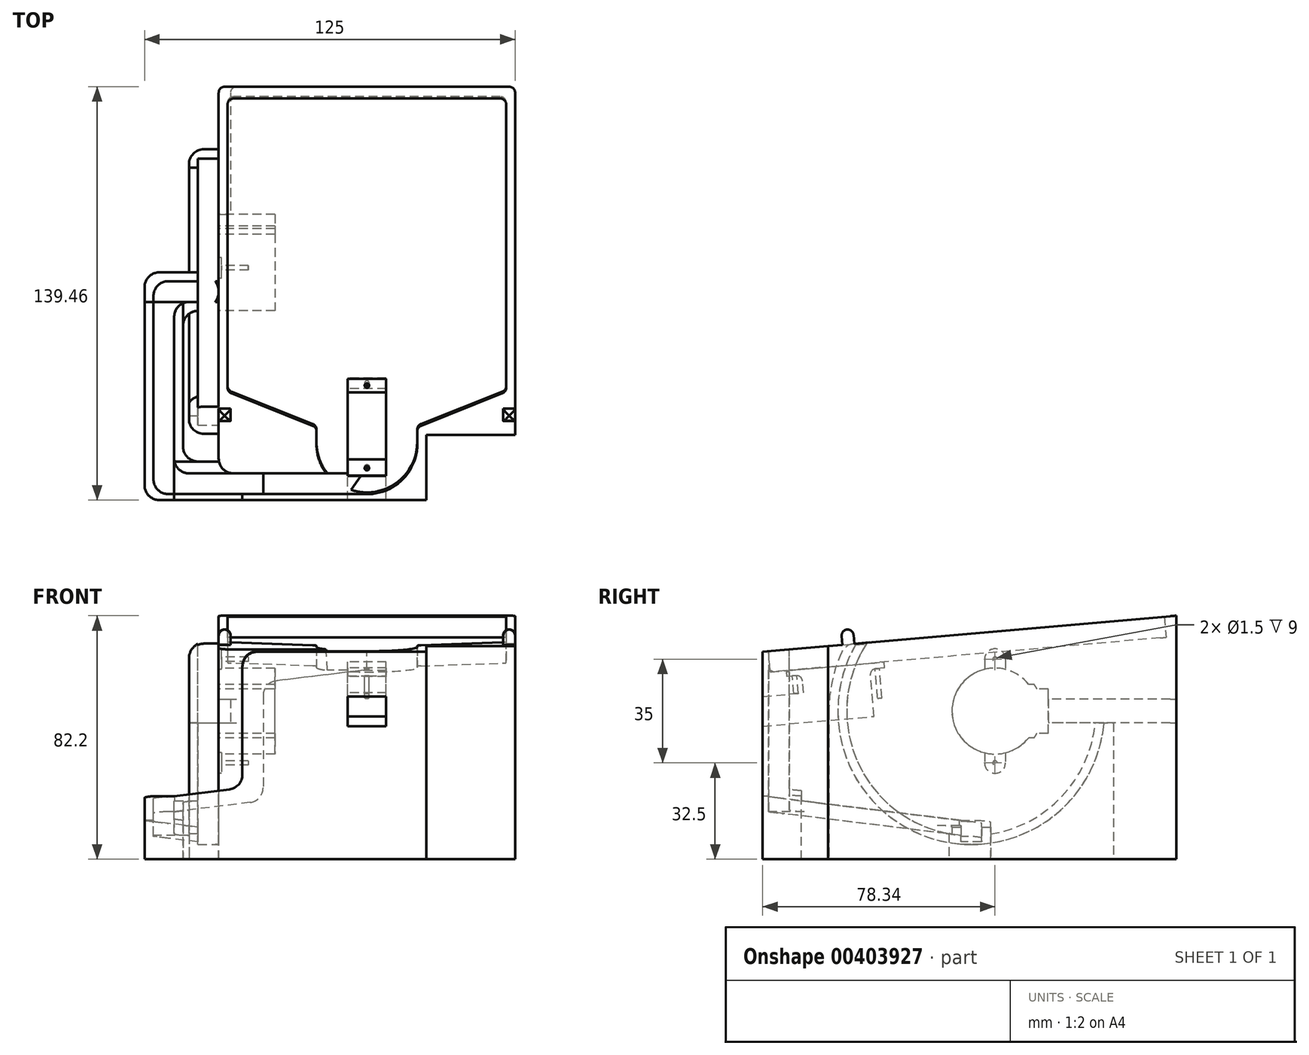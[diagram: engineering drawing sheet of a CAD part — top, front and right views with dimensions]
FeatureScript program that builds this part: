
annotation { "Feature Type Name" : "Feature", "Feature Type Description" : "" }
export const myFeature = defineFeature(function(context is Context, id is Id, definition is map)
    precondition{}
    {
        {
            var Q0;
            Q0=qCreatedBy(makeId("Right.planeOp"),FACE);
            var sketch = newSketch(context, id + "F0", { "sketchPlane" : qUnion([Q0])});
            skLineSegment(sketch, "E0", {"start": v(-65.34, 50) * mm, "end": v(-65.34, -20) * mm});
            skLineSegment(sketch, "E1", {"start": v(-65.34, -20) * mm, "end": v(74.12, -20) * mm});
            skLineSegment(sketch, "E2", {"start": v(74.12, -20) * mm, "end": v(74.12, 62.2) * mm});
            skLineSegment(sketch, "E3", {"start": v(74.12, 62.2) * mm, "end": v(-65.34, 50) * mm});
            skPoint(sketch, "E4", {"position": v(0, 55.72) * mm});
            skPoint(sketch, "E5", {"position": v(0, 48.7) * mm});
            skSolve(sketch);
        }
        {
            var Q0;
            Q0=qSketchRegion(id+"F0",true);
            extrude(context, id + "F1", {"entities" : qUnion([Q0]), "depth" : 50 * mm, "hasSecondDirection" : true, "secondDirectionOppositeDirection" : true, "secondDirectionDepth" : 50 * mm});
        }
        {
            var Q0;
            Q0=makeQuery(id+"F1.opExtrude","SWEPT_FACE",FACE,{"disambiguationData":[OSD([sQuery(id+"F0.wireOp",EDGE,"E3")])]});
            var sketch = newSketch(context, id + "F2", { "sketchPlane" : qUnion([Q0])});
            skPoint(sketch, "E6.endSnap0", {"position": v(0, -57.54) * mm});
            skPoint(sketch, "E6.end.orphan", {"position": v(0, -83) * mm});
            skPoint(sketch, "E7.orphan", {"position": v(-48, -57.54) * mm});
            skPoint(sketch, "E8.orphan", {"position": v(48, -57.54) * mm});
            skLineSegment(sketch, "E9.0", {"start": v(47, 75.26) * mm, "end": v(-47, 75.26) * mm});
            skLineSegment(sketch, "E9.1", {"start": v(47, 75.26) * mm, "end": v(47, -24.06) * mm});
            skLineSegment(sketch, "E9.2", {"start": v(-47, 75.26) * mm, "end": v(-47, -24.06) * mm});
            skLineSegment(sketch, "E9.3", {"start": v(17, -36.06) * mm, "end": v(47, -24.06) * mm});
            skLineSegment(sketch, "E9.4", {"start": v(-17, -36.06) * mm, "end": v(-47, -24.06) * mm});
            skLineSegment(sketch, "E9.5", {"start": v(-17, -41.74) * mm, "end": v(-17, -36.06) * mm});
            skArc(sketch, "E9.6", {"start": v(-17, -41.74) * mm, "mid": v(0, -58.74) * mm, "end": v(17, -41.74) * mm});
            skLineSegment(sketch, "E9.7", {"start": v(17, -41.74) * mm, "end": v(17, -36.06) * mm});
            skPoint(sketch, "E10.bottom.end.orphan", {"position": v(-48, 78.46) * mm});
            skPoint(sketch, "E10.bottom.start.orphan", {"position": v(48, 78.46) * mm});
            skPoint(sketch, "E11", {"position": v(0, 4.86) * mm});
            skSolve(sketch);
        }
        {
            var Q0;
            Q0=makeQuery(id+"F2.imprint","IMPRINT",FACE,{"disambiguationData":[TD([[makeQuery(id+"F2.imprint","IMPRINT",EDGE,{"derivedFrom":sQuery(id+"F2.wireOp",EDGE,"E9.0")}),1.0]])]});
            cPlane(context, id + "F3", {"entities" : qUnion([Q0]), "cplaneType" : CPlaneType.OFFSET, "offset" : 7 * mm, "oppositeDirection" : true, "width" : 150 * mm, "height" : 150 * mm});
        }
        {
            var Q0;
            Q0=qCreatedBy(id+"F3.planeOp",FACE);
            var sketch = newSketch(context, id + "F4", { "sketchPlane" : qUnion([Q0])});
            skPoint(sketch, "E12", {"position": v(0, 4.24) * mm});
            skPoint(sketch, "E13.endSnap0", {"position": v(0, -58.41) * mm});
            skPoint(sketch, "E13.end.orphan", {"position": v(0, -83.88) * mm});
            skPoint(sketch, "E14.orphan", {"position": v(-48, -58.41) * mm});
            skPoint(sketch, "E15.orphan", {"position": v(48, -58.41) * mm});
            skLineSegment(sketch, "E16.0", {"start": v(47, 75.26) * mm, "end": v(-47, 75.26) * mm});
            skLineSegment(sketch, "E16.1", {"start": v(47, 75.26) * mm, "end": v(47, -24.06) * mm});
            skLineSegment(sketch, "E16.2", {"start": v(-47, 75.26) * mm, "end": v(-47, -24.06) * mm});
            skLineSegment(sketch, "E16.3", {"start": v(17, -36.06) * mm, "end": v(47, -24.06) * mm});
            skLineSegment(sketch, "E16.4", {"start": v(-17, -36.06) * mm, "end": v(-47, -24.06) * mm});
            skLineSegment(sketch, "E16.5", {"start": v(-17, -41.74) * mm, "end": v(-17, -36.06) * mm});
            skArc(sketch, "E16.6", {"start": v(-17, -41.74) * mm, "mid": v(0, -58.74) * mm, "end": v(17, -41.74) * mm});
            skLineSegment(sketch, "E16.7", {"start": v(17, -41.74) * mm, "end": v(17, -36.06) * mm});
            skPoint(sketch, "E17.bottom.end.orphan", {"position": v(-48, 77.59) * mm});
            skPoint(sketch, "E17.bottom.start.orphan", {"position": v(48, 77.59) * mm});
            skSolve(sketch);
        }
        {
            var Q1;
            Q1=qSketchRegion(id+"F2",true);
            var Q2;
            Q2=qSketchRegion(id+"F4",true);
            loft(context, id + "F5", {"operationType" : NewBodyOperationType.REMOVE, "sheetProfilesArray" : [{ "sheetProfileEntities" : qUnion([Q1]) }, { "sheetProfileEntities" : qUnion([Q2]) }]});
        }
        {
            var Q0;
            Q0=makeQuery(id+"F1.opExtrude","CAP_FACE",FACE,{"disambiguationData":[OSD([sQuery(id+"F0.wireOp",EDGE,"E0"),sQuery(id+"F0.wireOp",EDGE,"E1"),sQuery(id+"F0.wireOp",EDGE,"E2"),sQuery(id+"F0.wireOp",EDGE,"E3")])],"isStart":true});
            var sketch = newSketch(context, id + "F6", { "sketchPlane" : qUnion([Q0])});
            skArc(sketch, "E18", {"start": v(-24.37, 21) * mm, "mid": v(1.5, 30) * mm, "end": v(-24.37, 39) * mm});
            skPoint(sketch, "E19", {"position": v(-5, 30) * mm});
            skLineSegment(sketch, "E20.bottom", {"start": v(-31, 22.5) * mm, "end": v(-27.13, 22.5) * mm});
            skLineSegment(sketch, "E20.top", {"start": v(-31, 37.5) * mm, "end": v(-27.13, 37.5) * mm});
            skLineSegment(sketch, "E20.left", {"start": v(-31, 22.5) * mm, "end": v(-31, 37.5) * mm});
            skArc(sketch, "E21", {"start": v(-26.23, 39) * mm, "mid": v(-26.7, 38.26) * mm, "end": v(-27.13, 37.5) * mm});
            skLineSegment(sketch, "E22.bottom", {"start": v(-26.23, 39) * mm, "end": v(-24.37, 39) * mm});
            skLineSegment(sketch, "E22.top", {"start": v(-26.23, 21) * mm, "end": v(-24.37, 21) * mm});
            skArc(sketch, "E23.trimOffspring", {"start": v(-27.13, 22.5) * mm, "mid": v(-26.7, 21.74) * mm, "end": v(-26.23, 21) * mm});
            skSolve(sketch);
        }
        {
            var Q0;
            Q0=qSketchRegion(id+"F6",true);
            extrude(context, id + "F7", {"entities" : qUnion([Q0]), "operationType" : NewBodyOperationType.REMOVE, "oppositeDirection" : true, "depth" : 19 * mm});
        }
        {
            var Q0;
            Q0=makeQuery(id+"F1.opExtrude","CAP_FACE",FACE,{"disambiguationData":[OSD([sQuery(id+"F0.wireOp",EDGE,"E0"),sQuery(id+"F0.wireOp",EDGE,"E1"),sQuery(id+"F0.wireOp",EDGE,"E2"),sQuery(id+"F0.wireOp",EDGE,"E3")])],"isStart":true});
            var sketch = newSketch(context, id + "F8", { "sketchPlane" : qUnion([Q0])});
            skLineSegment(sketch, "E24", {"start": v(-13, 47.5) * mm, "end": v(-13, 12.5) * mm});
            skPoint(sketch, "E25", {"position": v(-13, 30) * mm});
            skArc(sketch, "E26.0.startCap", {"start": v(-16.5, 47.5) * mm, "mid": v(-13, 51) * mm, "end": v(-9.5, 47.5) * mm});
            skArc(sketch, "E26.0.endCap", {"start": v(-9.5, 12.5) * mm, "mid": v(-13, 9) * mm, "end": v(-16.5, 12.5) * mm});
            skLineSegment(sketch, "E26.0.left", {"start": v(-9.5, 47.5) * mm, "end": v(-9.5, 12.5) * mm});
            skLineSegment(sketch, "E26.0.right", {"start": v(-16.5, 47.5) * mm, "end": v(-16.5, 12.5) * mm});
            skSolve(sketch);
        }
        {
            var Q0;
            Q0=qSketchRegion(id+"F8",true);
            extrude(context, id + "F9", {"entities" : qUnion([Q0]), "operationType" : NewBodyOperationType.REMOVE, "oppositeDirection" : true, "depth" : 1 * mm});
        }
        {
            var Q0;
            Q0=makeQuery(id+"F1.opExtrude","CAP_FACE",FACE,{"disambiguationData":[OSD([sQuery(id+"F0.wireOp",EDGE,"E0"),sQuery(id+"F0.wireOp",EDGE,"E1"),sQuery(id+"F0.wireOp",EDGE,"E2"),sQuery(id+"F0.wireOp",EDGE,"E3")])],"isStart":true});
            var sketch = newSketch(context, id + "F10", { "sketchPlane" : qUnion([Q0])});
            skLineSegment(sketch, "E27.bottom", {"start": v(-81, 34) * mm, "end": v(-21, 34) * mm});
            skLineSegment(sketch, "E27.top", {"start": v(-81, 26) * mm, "end": v(-21, 26) * mm});
            skLineSegment(sketch, "E27.left", {"start": v(-81, 34) * mm, "end": v(-81, 26) * mm});
            skLineSegment(sketch, "E27.right", {"start": v(-21, 34) * mm, "end": v(-21, 26) * mm});
            skPoint(sketch, "E27.middle", {"position": v(-51, 30) * mm});
            skSolve(sketch);
        }
        {
            var Q0;
            Q0=qSketchRegion(id+"F10",true);
            extrude(context, id + "F11", {"entities" : qUnion([Q0]), "operationType" : NewBodyOperationType.REMOVE, "oppositeDirection" : true, "depth" : 4 * mm});
        }
        {
            var Q0;
            Q0=qCreatedBy(makeId("Front.planeOp"),FACE);
            cPlane(context, id + "F12", {"entities" : qUnion([Q0]), "cplaneType" : CPlaneType.OFFSET, "offset" : 5 * mm, "oppositeDirection" : true, "width" : 150 * mm, "height" : 150 * mm});
        }
        {
            var Q0;
            Q0=qCreatedBy(id+"F12.planeOp",FACE);
            var sketch = newSketch(context, id + "F13", { "sketchPlane" : qUnion([Q0])});
            skLineSegment(sketch, "E28", {"start": v(-50, -20) * mm, "end": v(-75, -20) * mm});
            skLineSegment(sketch, "E29", {"start": v(-50, -9.96) * mm, "end": v(-75, -6.9) * mm});
            skLineSegment(sketch, "E30", {"start": v(-75, -20) * mm, "end": v(-75, -6.9) * mm});
            skLineSegment(sketch, "E31", {"start": v(-50, -20) * mm, "end": v(-50, -9.96) * mm});
            skSolve(sketch);
        }
        {
            var Q0;
            Q0=qSketchRegion(id+"F13",true);
            extrude(context, id + "F14", {"entities" : qUnion([Q0]), "operationType" : NewBodyOperationType.ADD, "depth" : 6.5 * mm, "hasSecondDirection" : true, "secondDirectionOppositeDirection" : true, "secondDirectionDepth" : 6.5 * mm});
        }
        {
            var Q0;
            Q0=makeQuery(id+"F2.imprint","IMPRINT",FACE,{"disambiguationData":[TD([[makeQuery(id+"F2.imprint","IMPRINT",EDGE,{"derivedFrom":sQuery(id+"F2.wireOp",EDGE,"E9.0")}),1.0]])]});
            var sketch = newSketch(context, id + "F15", { "sketchPlane" : qUnion([Q0])});
            skLineSegment(sketch, "E32.bottom", {"start": v(6.5, -48.24) * mm, "end": v(-6.5, -48.24) * mm});
            skLineSegment(sketch, "E32.top", {"start": v(6.5, -25.24) * mm, "end": v(-6.5, -25.24) * mm});
            skLineSegment(sketch, "E32.left", {"start": v(6.5, -48.24) * mm, "end": v(6.5, -25.24) * mm});
            skLineSegment(sketch, "E32.right", {"start": v(-6.5, -48.24) * mm, "end": v(-6.5, -25.24) * mm});
            skPoint(sketch, "E32.middle", {"position": v(0, -36.74) * mm});
            skSolve(sketch);
        }
        {
            var Q0;
            Q0=qSketchRegion(id+"F15",true);
            extrude(context, id + "F16", {"entities" : qUnion([Q0]), "operationType" : NewBodyOperationType.REMOVE, "oppositeDirection" : true, "depth" : 25 * mm});
        }
        {
            var Q0;
            Q0=makeQuery(id+"F2.imprint","IMPRINT",FACE,{"disambiguationData":[TD([[makeQuery(id+"F2.imprint","IMPRINT",EDGE,{"derivedFrom":sQuery(id+"F2.wireOp",EDGE,"E9.0")}),1.0]])]});
            var sketch = newSketch(context, id + "F17", { "sketchPlane" : qUnion([Q0])});
            skLineSegment(sketch, "E33.bottom", {"start": v(6.5, -20.24) * mm, "end": v(-6.5, -20.24) * mm});
            skLineSegment(sketch, "E33.top", {"start": v(6.5, -53.24) * mm, "end": v(-6.5, -53.24) * mm});
            skLineSegment(sketch, "E33.left", {"start": v(6.5, -20.24) * mm, "end": v(6.5, -53.24) * mm});
            skLineSegment(sketch, "E33.right", {"start": v(-6.5, -20.24) * mm, "end": v(-6.5, -53.24) * mm});
            skPoint(sketch, "E33.middle", {"position": v(0, -36.74) * mm});
            skSolve(sketch);
        }
        {
            var Q0;
            Q0=qSketchRegion(id+"F17",true);
            extrude(context, id + "F18", {"entities" : qUnion([Q0]), "operationType" : NewBodyOperationType.REMOVE, "oppositeDirection" : true, "depth" : 9 * mm});
        }
        {
            var Q0;
            Q0=makeQuery(id+"FUqeBeKpT4LYNuk_1.boolean.opBoolean","MERGE",FACE,{"derivedFrom":[makeQuery(id+"F1.opExtrude","SWEPT_FACE",FACE,{"disambiguationData":[OSD([sQuery(id+"F0.wireOp",EDGE,"E0")])]}),makeQuery(id+"F61UTTqEWsXgY2D_1.opExtrude","SWEPT_FACE",FACE,{"disambiguationData":[OSD([sQuery(id+"F9Du9WT9e9JY5Dl_1.wireOp",EDGE,"sJgd1tPc-9qsz-vVnT-TqeQ-4TYIqpoZbmCu")])]}),makeQuery(id+"FUqeBeKpT4LYNuk_1.opExtrude","CAP_FACE",FACE,{"disambiguationData":[OSD([sQuery(id+"Fu5qXJoa0auTo1w_1.wireOp",EDGE,"depduNjt-3aMR-BOii-vv3o-0Txvqa5xbjUM"),sQuery(id+"Fu5qXJoa0auTo1w_1.wireOp",EDGE,"YClS0oY7-eXia-WmQ4-NOUT-qmrgQAcRW2ul"),sQuery(id+"Fu5qXJoa0auTo1w_1.wireOp",EDGE,"FjPESpCu-MEkZ-X1k0-rLkk-jPPFp3MV8du9"),sQuery(id+"Fu5qXJoa0auTo1w_1.wireOp",EDGE,"T3NzeVoH-fv4R-7HJz-S144-zwuEIWOQCuFN")])],"isStart":true})]});
            var sketch = newSketch(context, id + "F19", { "sketchPlane" : qUnion([Q0])});
            skLineSegment(sketch, "E34.bottom", {"start": v(50, -20) * mm, "end": v(20, -20) * mm});
            skLineSegment(sketch, "E34.top", {"start": v(50, 60) * mm, "end": v(20, 60) * mm});
            skLineSegment(sketch, "E34.left", {"start": v(50, -20) * mm, "end": v(50, 60) * mm});
            skLineSegment(sketch, "E34.right", {"start": v(20, -20) * mm, "end": v(20, 60) * mm});
            skSolve(sketch);
        }
        {
            var Q0;
            Q0=qSketchRegion(id+"F19",true);
            extrude(context, id + "F20", {"entities" : qUnion([Q0]), "operationType" : NewBodyOperationType.REMOVE, "oppositeDirection" : true, "depth" : 22 * mm});
        }
        {
            var Q0;
            Q0=makeQuery(id+"F16.boolean.opBoolean","COPY",FACE,{"derivedFrom":makeQuery(id+"F16.opExtrude","SWEPT_FACE",FACE,{"disambiguationData":[OSD([sQuery(id+"F15.wireOp",EDGE,"E32.bottom")])]})});
            var sketch = newSketch(context, id + "F21", { "sketchPlane" : qUnion([Q0])});
            skLineSegment(sketch, "E35.bottom", {"start": v(-6.5, 30.5) * mm, "end": v(6.5, 30.5) * mm});
            skLineSegment(sketch, "E35.top", {"start": v(-6.5, 40.5) * mm, "end": v(6.5, 40.5) * mm});
            skLineSegment(sketch, "E35.left", {"start": v(-6.5, 30.5) * mm, "end": v(-6.5, 40.5) * mm});
            skLineSegment(sketch, "E35.right", {"start": v(6.5, 30.5) * mm, "end": v(6.5, 40.5) * mm});
            skSolve(sketch);
        }
        {
            var Q0;
            Q0=qSketchRegion(id+"F21",true);
            extrude(context, id + "F22", {"entities" : qUnion([Q0]), "operationType" : NewBodyOperationType.REMOVE, "oppositeDirection" : true, "depth" : 25 * mm});
        }
        {
            var Q0;
            Q0=qCreatedBy(id+"F12.planeOp",FACE);
            var sketch = newSketch(context, id + "F23", { "sketchPlane" : qUnion([Q0])});
            skLineSegment(sketch, "E36", {"start": v(-50, -6.3) * mm, "end": v(-50, -15) * mm});
            skLineSegment(sketch, "E37", {"start": v(-50, -15) * mm, "end": v(-72, -12.3) * mm});
            skLineSegment(sketch, "E38", {"start": v(-72, -12.3) * mm, "end": v(-72, -6.3) * mm});
            skLineSegment(sketch, "E39", {"start": v(-72, -6.3) * mm, "end": v(-50, -6.3) * mm});
            skSolve(sketch);
        }
        {
            var Q0;
            Q0=qSketchRegion(id+"F23",true);
            extrude(context, id + "F24", {"entities" : qUnion([Q0]), "operationType" : NewBodyOperationType.REMOVE, "oppositeDirection" : true, "depth" : 3.5 * mm, "hasSecondDirection" : true, "secondDirectionOppositeDirection" : false, "secondDirectionDepth" : 3.5 * mm});
        }
        {
            var Q0;
            Q0=makeQuery(id+"F14.opExtrude","SWEPT_FACE",FACE,{"disambiguationData":[OSD([sQuery(id+"F13.wireOp",EDGE,"E30")])]});
            var sketch = newSketch(context, id + "F25", { "sketchPlane" : qUnion([Q0])});
            skLineSegment(sketch, "E40", {"start": v(1.5, -20) * mm, "end": v(65.34, -20) * mm});
            skLineSegment(sketch, "E41", {"start": v(65.34, -20) * mm, "end": v(65.34, 1.31) * mm});
            skLineSegment(sketch, "E42", {"start": v(65.34, 1.31) * mm, "end": v(-1.5, -6.9) * mm});
            skLineSegment(sketch, "E43", {"start": v(-1.5, -6.9) * mm, "end": v(-1.5, -20) * mm});
            skLineSegment(sketch, "E44", {"start": v(-1.5, -20) * mm, "end": v(1.5, -20) * mm});
            skSolve(sketch);
        }
        {
            var Q0;
            Q0=qSketchRegion(id+"F25",true);
            extrude(context, id + "F26", {"entities" : qUnion([Q0]), "operationType" : NewBodyOperationType.ADD, "oppositeDirection" : true, "depth" : 13 * mm});
        }
        {
            var Q0;
            Q0=makeQuery(id+"F26.boolean.opBoolean","MERGE",FACE,{"derivedFrom":[makeQuery(id+"F14.opExtrude","SWEPT_FACE",FACE,{"disambiguationData":[OSD([sQuery(id+"F13.wireOp",EDGE,"E30")])]}),makeQuery(id+"F26.opExtrude","CAP_FACE",FACE,{"disambiguationData":[OSD([sQuery(id+"F25.wireOp",EDGE,"E40"),sQuery(id+"F25.wireOp",EDGE,"E41"),sQuery(id+"F25.wireOp",EDGE,"E42"),sQuery(id+"F25.wireOp",EDGE,"E43"),sQuery(id+"F25.wireOp",EDGE,"E44")])],"isStart":true})]});
            cPlane(context, id + "F27", {"entities" : qUnion([Q0]), "cplaneType" : CPlaneType.OFFSET, "offset" : 3 * mm, "oppositeDirection" : true, "width" : 150 * mm, "height" : 150 * mm});
        }
        {
            var Q0;
            Q0=qCreatedBy(id+"F27.planeOp",FACE);
            var sketch = newSketch(context, id + "F28", { "sketchPlane" : qUnion([Q0])});
            skLineSegment(sketch, "E45", {"start": v(-1.5, -2.4) * mm, "end": v(-1.5, -11.93) * mm});
            skLineSegment(sketch, "E46", {"start": v(-1.5, -11.93) * mm, "end": v(63.34, -3.97) * mm});
            skLineSegment(sketch, "E47", {"start": v(63.34, -3.97) * mm, "end": v(63.34, 3.33) * mm});
            skLineSegment(sketch, "E48", {"start": v(63.34, 3.33) * mm, "end": v(-1.5, 3.33) * mm});
            skLineSegment(sketch, "E49", {"start": v(-1.5, 3.33) * mm, "end": v(-1.5, -2.4) * mm});
            skSolve(sketch);
        }
        {
            var Q0;
            Q0=qSketchRegion(id+"F28",true);
            extrude(context, id + "F29", {"entities" : qUnion([Q0]), "operationType" : NewBodyOperationType.REMOVE, "oppositeDirection" : true, "depth" : 7 * mm});
        }
        {
            var Q0;
            Q0=makeQuery(id+"F1.opExtrude","SWEPT_FACE",FACE,{"disambiguationData":[OSD([sQuery(id+"F0.wireOp",EDGE,"E0")])]});
            var sketch = newSketch(context, id + "F30", { "sketchPlane" : qUnion([Q0])});
            skLineSegment(sketch, "E50", {"start": v(-50, -20) * mm, "end": v(-50, 3.16) * mm});
            skLineSegment(sketch, "E51", {"start": v(-50, 3.16) * mm, "end": v(-65, 1.31) * mm});
            skLineSegment(sketch, "E52", {"start": v(-65, 1.31) * mm, "end": v(-65, -20) * mm});
            skLineSegment(sketch, "E53", {"start": v(-65, -20) * mm, "end": v(-50, -20) * mm});
            skSolve(sketch);
        }
        {
            var Q0;
            Q0=qSketchRegion(id+"F30",true);
            extrude(context, id + "F31", {"entities" : qUnion([Q0]), "operationType" : NewBodyOperationType.ADD, "oppositeDirection" : true, "depth" : 13 * mm});
        }
        {
            var Q0;
            Q0=makeQuery(id+"F29.boolean.opBoolean","COPY",FACE,{"derivedFrom":makeQuery(id+"F29.opExtrude","SWEPT_FACE",FACE,{"disambiguationData":[OSD([sQuery(id+"F28.wireOp",EDGE,"E47")])]})});
            var sketch = newSketch(context, id + "F32", { "sketchPlane" : qUnion([Q0])});
            skLineSegment(sketch, "E54", {"start": v(65, -3.97) * mm, "end": v(65, 76.03) * mm});
            skLineSegment(sketch, "E55", {"start": v(65, 76.03) * mm, "end": v(0, 76.03) * mm});
            skLineSegment(sketch, "E56", {"start": v(0, 76.03) * mm, "end": v(0, 43.93) * mm});
            skLineSegment(sketch, "E57", {"start": v(0, 43.93) * mm, "end": v(35, 39.63) * mm});
            skLineSegment(sketch, "E58", {"start": v(35, 39.63) * mm, "end": v(35, -0.29) * mm});
            skLineSegment(sketch, "E59", {"start": v(35, -0.29) * mm, "end": v(65, -3.97) * mm});
            skSolve(sketch);
        }
        {
            var Q0;
            Q0=qSketchRegion(id+"F32",true);
            extrude(context, id + "F33", {"entities" : qUnion([Q0]), "operationType" : NewBodyOperationType.REMOVE, "depth" : 7 * mm});
        }
        {
            var Q0;
            Q0=makeQuery(id+"F33.boolean.opBoolean","MERGE",FACE,{"derivedFrom":[makeQuery(id+"F29.boolean.opBoolean","COPY",FACE,{"derivedFrom":makeQuery(id+"F29.opExtrude","SWEPT_FACE",FACE,{"disambiguationData":[OSD([sQuery(id+"F28.wireOp",EDGE,"E47")])]})}),makeQuery(id+"F33.opExtrude","CAP_FACE",FACE,{"disambiguationData":[OSD([sQuery(id+"F32.wireOp",EDGE,"E54"),sQuery(id+"F32.wireOp",EDGE,"E55"),sQuery(id+"F32.wireOp",EDGE,"E56"),sQuery(id+"F32.wireOp",EDGE,"E57"),sQuery(id+"F32.wireOp",EDGE,"E58"),sQuery(id+"F32.wireOp",EDGE,"E59")])],"isStart":true})]});
            var sketch = newSketch(context, id + "F34", { "sketchPlane" : qUnion([Q0])});
            skLineSegment(sketch, "E60", {"start": v(50, 3.16) * mm, "end": v(42, 4.14) * mm});
            skLineSegment(sketch, "E61", {"start": v(42, 4.14) * mm, "end": v(42, 50.17) * mm});
            skLineSegment(sketch, "E62", {"start": v(42, 50.17) * mm, "end": v(50, 50.17) * mm});
            skLineSegment(sketch, "E63", {"start": v(50, 50.17) * mm, "end": v(50, 3.16) * mm});
            skSolve(sketch);
        }
        {
            var Q0;
            Q0=qSketchRegion(id+"F34",true);
            extrude(context, id + "F35", {"entities" : qUnion([Q0]), "operationType" : NewBodyOperationType.REMOVE, "oppositeDirection" : true, "depth" : 3 * mm});
        }
        {
            var Q0;
            Q0=makeQuery(id+"F6.imprint","IMPRINT",FACE,{"disambiguationData":[TD([[makeQuery(id+"F6.imprint","IMPRINT",EDGE,{"derivedFrom":sQuery(id+"F6.wireOp",EDGE,"E18")}),-1.0]])]});
            var sketch = newSketch(context, id + "F36", { "sketchPlane" : qUnion([Q0])});
            skArc(sketch, "E64", {"start": v(-49.82, 26) * mm, "mid": v(-37.7, -0.92) * mm, "end": v(-11.5, -14.53) * mm});
            skArc(sketch, "E65", {"start": v(43, 30) * mm, "mid": v(41.59, 41.56) * mm, "end": v(37.43, 52.44) * mm});
            skLineSegment(sketch, "E66", {"start": v(37.43, 52.44) * mm, "end": v(33.82, 52.76) * mm});
            skPoint(sketch, "E67", {"position": v(43, 30) * mm});
            skLineSegment(sketch, "E68", {"start": v(43, 30) * mm, "end": v(43, -20) * mm});
            skLineSegment(sketch, "E69", {"start": v(-53, 26) * mm, "end": v(-53, -20) * mm});
            skLineSegment(sketch, "E70", {"start": v(-53, -20) * mm, "end": v(43, -20) * mm});
            skLineSegment(sketch, "E71", {"start": v(-53, 26) * mm, "end": v(-49.82, 26) * mm});
            skLineSegment(sketch, "E72", {"start": v(-11.5, -14.53) * mm, "end": v(-11.5, -20) * mm});
            skLineSegment(sketch, "E73", {"start": v(1.5, -14.53) * mm, "end": v(1.5, -20) * mm});
            skArc(sketch, "E74.trimOffspring", {"start": v(1.5, -14.53) * mm, "mid": v(35.56, 10.52) * mm, "end": v(33.82, 52.76) * mm});
            skSolve(sketch);
        }
        {
            var Q0;
            Q0=qSketchRegion(id+"F36",true);
            extrude(context, id + "F37", {"entities" : qUnion([Q0]), "operationType" : NewBodyOperationType.ADD, "depth" : 10 * mm});
        }
        {
            var Q0;
            Q0=makeQuery(id+"F37.opExtrude","CAP_FACE",FACE,{"disambiguationData":[OSD([sQuery(id+"F36.wireOp",EDGE,"E64"),sQuery(id+"F36.wireOp",EDGE,"E69"),sQuery(id+"F36.wireOp",EDGE,"E70"),sQuery(id+"F36.wireOp",EDGE,"E71"),sQuery(id+"F36.wireOp",EDGE,"E72")])],"isStart":false});
            var sketch = newSketch(context, id + "F38", { "sketchPlane" : qUnion([Q0])});
            skArc(sketch, "E75", {"start": v(1.5, -14.53) * mm, "mid": v(35.56, 10.52) * mm, "end": v(33.82, 52.76) * mm});
            skArc(sketch, "E76", {"start": v(1.5, -11.5) * mm, "mid": v(33.4, 13) * mm, "end": v(30.09, 53.08) * mm});
            skLineSegment(sketch, "E77", {"start": v(-49.82, 26) * mm, "end": v(-46.8, 26) * mm});
            skLineSegment(sketch, "E78", {"start": v(33.82, 52.76) * mm, "end": v(30.09, 53.08) * mm});
            skLineSegment(sketch, "E79", {"start": v(-11.5, -14.53) * mm, "end": v(-11.5, -11.5) * mm});
            skLineSegment(sketch, "E80", {"start": v(1.5, -14.53) * mm, "end": v(1.5, -11.5) * mm});
            skArc(sketch, "E81.trimOffspring", {"start": v(-46.8, 26) * mm, "mid": v(-35.58, 1.2) * mm, "end": v(-11.5, -11.5) * mm});
            skArc(sketch, "E82.trimOffspring", {"start": v(-49.82, 26) * mm, "mid": v(-37.7, -0.92) * mm, "end": v(-11.5, -14.53) * mm});
            skSolve(sketch);
        }
        {
            var Q0;
            Q0=qSketchRegion(id+"F38",true);
            extrude(context, id + "F39", {"entities" : qUnion([Q0]), "operationType" : NewBodyOperationType.ADD, "oppositeDirection" : true, "depth" : 3 * mm});
        }
        {
            var Q0;
            Q0=makeQuery(id+"F6.imprint","IMPRINT",FACE,{"disambiguationData":[TD([[makeQuery(id+"F6.imprint","IMPRINT",EDGE,{"derivedFrom":sQuery(id+"F6.wireOp",EDGE,"E18")}),-1.0]])]});
            var sketch = newSketch(context, id + "F40", { "sketchPlane" : qUnion([Q0])});
            skCircle(sketch, "E83", {"center": v(-5, 30) * mm, "radius": 45 * mm});
            skSolve(sketch);
        }
        {
            var Q0;
            Q0=qSketchRegion(id+"F40",true);
            extrude(context, id + "F41", {"entities" : qUnion([Q0]), "operationType" : NewBodyOperationType.REMOVE, "depth" : 7 * mm});
        }
        {
            var Q0;
            Q0=makeQuery(id+"F20.boolean.opBoolean","COPY",EDGE,{"derivedFrom":makeQuery(id+"F20.opExtrude","CAP_EDGE",EDGE,{"disambiguationData":[OSD([sQuery(id+"F19.wireOp",EDGE,"E34.right")])],"isStart":true})});
            var Q1;
            Q1=makeQuery(id+"F20.boolean.opBoolean","COPY",EDGE,{"derivedFrom":makeQuery(id+"F20.opExtrude","CAP_EDGE",EDGE,{"disambiguationData":[OSD([sQuery(id+"F19.wireOp",EDGE,"E34.left")])],"isStart":false})});
            var Q2;
            Q2=makeQuery(id+"F37.opExtrude","CAP_EDGE",EDGE,{"disambiguationData":[OSD([sQuery(id+"F36.wireOp",EDGE,"E69")])],"isStart":false});
            var Q3;
            Q3=makeQuery(id+"F37.opExtrude","CAP_EDGE",EDGE,{"disambiguationData":[OSD([sQuery(id+"F36.wireOp",EDGE,"E68")])],"isStart":false});
            var Q4;
            Q4=makeQuery(id+"F37.opExtrude","SWEPT_EDGE",EDGE,{"disambiguationData":[OSD([sQuery(id+"F0.wireOp",EDGE,"E3"),sQuery(id+"F36.wireOp",EDGE,"E65"),sQuery(id+"F36.wireOp",EDGE,"E66")])]});
            var Q5;
            Q5=makeQuery(id+"F39.boolean.opBoolean","MERGE",EDGE,{"derivedFrom":[makeQuery(id+"F37.opExtrude","CAP_EDGE",EDGE,{"disambiguationData":[OSD([sQuery(id+"F36.wireOp",EDGE,"E66")])],"isStart":false}),makeQuery(id+"F39.opExtrude","CAP_EDGE",EDGE,{"disambiguationData":[OSD([sQuery(id+"F38.wireOp",EDGE,"E78")])],"isStart":true})]});
            var Q6;
            Q6=makeQuery(id+"F14.opExtrude","CAP_EDGE",EDGE,{"disambiguationData":[OSD([sQuery(id+"F13.wireOp",EDGE,"E30")])],"isStart":true});
            var Q7;
            Q7=makeQuery(id+"F26.opExtrude","CAP_EDGE",EDGE,{"disambiguationData":[OSD([sQuery(id+"F25.wireOp",EDGE,"E41")])],"isStart":true});
            var Q8;
            Q8=makeQuery(id+"F35.boolean.opBoolean","INTERSECT",EDGE,{"derivedFrom":[makeQuery(id+"F1.opExtrude","SWEPT_FACE",FACE,{"disambiguationData":[OSD([sQuery(id+"F0.wireOp",EDGE,"E3")])]}),makeQuery(id+"F35.opExtrude","SWEPT_FACE",FACE,{"disambiguationData":[OSD([sQuery(id+"F34.wireOp",EDGE,"E61")])]})]});
            var Q9;
            Q9=makeQuery(id+"F33.boolean.opBoolean","COPY",EDGE,{"derivedFrom":makeQuery(id+"F33.opExtrude","CAP_EDGE",EDGE,{"disambiguationData":[OSD([sQuery(id+"F32.wireOp",EDGE,"E54")])],"isStart":false})});
            var Q10;
            Q10=makeQuery(id+"F31.boolean.opBoolean","INTERSECT",EDGE,{"derivedFrom":[makeQuery(id+"F26.opExtrude","CAP_FACE",FACE,{"disambiguationData":[OSD([sQuery(id+"F25.wireOp",EDGE,"E40"),sQuery(id+"F25.wireOp",EDGE,"E41"),sQuery(id+"F25.wireOp",EDGE,"E42"),sQuery(id+"F25.wireOp",EDGE,"E43"),sQuery(id+"F25.wireOp",EDGE,"E44")])],"isStart":false}),makeQuery(id+"F31.opExtrude","CAP_FACE",FACE,{"disambiguationData":[OSD([sQuery(id+"F30.wireOp",EDGE,"E50"),sQuery(id+"F30.wireOp",EDGE,"E51"),sQuery(id+"F30.wireOp",EDGE,"E52"),sQuery(id+"F30.wireOp",EDGE,"E53")])],"isStart":false})]});
            var Q11;
            Q11=makeQuery(id+"F29.boolean.opBoolean","COPY",EDGE,{"derivedFrom":makeQuery(id+"F29.opExtrude","CAP_EDGE",EDGE,{"disambiguationData":[OSD([sQuery(id+"F28.wireOp",EDGE,"E47")])],"isStart":true})});
            var Q12;
            Q12=makeQuery(id+"F26.boolean.opBoolean","INTERSECT",EDGE,{"derivedFrom":[makeQuery(id+"F14.opExtrude","CAP_FACE",FACE,{"disambiguationData":[OSD([sQuery(id+"F13.wireOp",EDGE,"E28"),sQuery(id+"F13.wireOp",EDGE,"E29"),sQuery(id+"F13.wireOp",EDGE,"E30"),sQuery(id+"F13.wireOp",EDGE,"E31")])],"isStart":false}),makeQuery(id+"F26.opExtrude","CAP_FACE",FACE,{"disambiguationData":[OSD([sQuery(id+"F25.wireOp",EDGE,"E40"),sQuery(id+"F25.wireOp",EDGE,"E41"),sQuery(id+"F25.wireOp",EDGE,"E42"),sQuery(id+"F25.wireOp",EDGE,"E43"),sQuery(id+"F25.wireOp",EDGE,"E44")])],"isStart":false})]});
            var Q13;
            Q13=makeQuery(id+"F24.boolean.opBoolean","COPY",EDGE,{"derivedFrom":makeQuery(id+"F24.opExtrude","CAP_EDGE",EDGE,{"disambiguationData":[OSD([sQuery(id+"F23.wireOp",EDGE,"E38")])],"isStart":false})});
            var Q14;
            Q14=makeQuery(id+"F29.boolean.opBoolean","COPY",EDGE,{"derivedFrom":makeQuery(id+"F29.opExtrude","CAP_EDGE",EDGE,{"disambiguationData":[OSD([sQuery(id+"F28.wireOp",EDGE,"E45"),sQuery(id+"F28.wireOp",EDGE,"E49")])],"isStart":false})});
            var Q15;
            Q15=makeQuery(id+"F35.boolean.opBoolean","COPY",EDGE,{"derivedFrom":makeQuery(id+"F35.opExtrude","SWEPT_EDGE",EDGE,{"disambiguationData":[OSD([sQuery(id+"F34.wireOp",EDGE,"E60"),sQuery(id+"F34.wireOp",EDGE,"E61")])]})});
            var Q16;
            Q16=makeQuery(id+"F33.boolean.opBoolean","COPY",EDGE,{"derivedFrom":makeQuery(id+"F33.opExtrude","SWEPT_EDGE",EDGE,{"disambiguationData":[OSD([sQuery(id+"F32.wireOp",EDGE,"E57"),sQuery(id+"F32.wireOp",EDGE,"E58")])]})});
            var Q17;
            Q17=makeQuery(id+"F33.boolean.opBoolean","COPY",EDGE,{"derivedFrom":makeQuery(id+"F33.opExtrude","SWEPT_EDGE",EDGE,{"disambiguationData":[OSD([sQuery(id+"F32.wireOp",EDGE,"E58"),sQuery(id+"F32.wireOp",EDGE,"E59")])]})});
            var Q18;
            Q18=makeQuery(id+"F33.boolean.opBoolean","INTERSECT",EDGE,{"derivedFrom":[makeQuery(id+"F24.boolean.opBoolean","MERGE",FACE,{"derivedFrom":[makeQuery(id+"F1.opExtrude","CAP_FACE",FACE,{"disambiguationData":[OSD([sQuery(id+"F0.wireOp",EDGE,"E0"),sQuery(id+"F0.wireOp",EDGE,"E1"),sQuery(id+"F0.wireOp",EDGE,"E2"),sQuery(id+"F0.wireOp",EDGE,"E3")])],"isStart":true}),makeQuery(id+"F24.opExtrude","SWEPT_FACE",FACE,{"disambiguationData":[OSD([sQuery(id+"F23.wireOp",EDGE,"E36")])]})]}),makeQuery(id+"F33.opExtrude","CAP_FACE",FACE,{"disambiguationData":[OSD([sQuery(id+"F32.wireOp",EDGE,"E54"),sQuery(id+"F32.wireOp",EDGE,"E55"),sQuery(id+"F32.wireOp",EDGE,"E56"),sQuery(id+"F32.wireOp",EDGE,"E57"),sQuery(id+"F32.wireOp",EDGE,"E58"),sQuery(id+"F32.wireOp",EDGE,"E59")])],"isStart":false})]});
            fillet(context, id + "F42", {"entities" : qUnion([Q0, Q1, Q2, Q3, Q4, Q5, Q6, Q7, Q8, Q9, Q10, Q11, Q12, Q13, Q14, Q15, Q16, Q17, Q18]), "radius" : 5 * mm, "tangentPropagation" : true, "allowEdgeOverflow" : false});
        }
        {
            var Q0;
            Q0=makeQuery(id+"F5.boolean.opBoolean","COPY",EDGE,{"derivedFrom":makeQuery(id+"F5.opLoft","SWEPT_EDGE",EDGE,{"disambiguationData":[OSD([sQuery(id+"F2.wireOp",EDGE,"E9.0"),sQuery(id+"F2.wireOp",EDGE,"E9.2"),sQuery(id+"F4.wireOp",EDGE,"E16.0"),sQuery(id+"F4.wireOp",EDGE,"E16.2")])]})});
            var Q1;
            Q1=makeQuery(id+"F5.boolean.opBoolean","COPY",EDGE,{"derivedFrom":makeQuery(id+"F5.opLoft","SWEPT_EDGE",EDGE,{"disambiguationData":[OSD([sQuery(id+"F2.wireOp",EDGE,"E9.0"),sQuery(id+"F2.wireOp",EDGE,"E9.1"),sQuery(id+"F4.wireOp",EDGE,"E16.0"),sQuery(id+"F4.wireOp",EDGE,"E16.1")])]})});
            var Q2;
            Q2=makeQuery(id+"F5.boolean.opBoolean","COPY",EDGE,{"derivedFrom":makeQuery(id+"F5.opLoft","SWEPT_EDGE",EDGE,{"disambiguationData":[OSD([sQuery(id+"F2.wireOp",EDGE,"E9.2"),sQuery(id+"F2.wireOp",EDGE,"E9.4"),sQuery(id+"F4.wireOp",EDGE,"E16.2"),sQuery(id+"F4.wireOp",EDGE,"E16.4")])]})});
            var Q3;
            Q3=makeQuery(id+"F5.boolean.opBoolean","COPY",EDGE,{"derivedFrom":makeQuery(id+"F5.opLoft","SWEPT_EDGE",EDGE,{"disambiguationData":[OSD([sQuery(id+"F2.wireOp",EDGE,"E9.1"),sQuery(id+"F2.wireOp",EDGE,"E9.3"),sQuery(id+"F4.wireOp",EDGE,"E16.1"),sQuery(id+"F4.wireOp",EDGE,"E16.3")])]})});
            var Q4;
            Q4=makeQuery(id+"F5.boolean.opBoolean","COPY",EDGE,{"derivedFrom":makeQuery(id+"F5.opLoft","SWEPT_EDGE",EDGE,{"disambiguationData":[OSD([sQuery(id+"F2.wireOp",EDGE,"E9.3"),sQuery(id+"F2.wireOp",EDGE,"E9.7"),sQuery(id+"F4.wireOp",EDGE,"E16.3"),sQuery(id+"F4.wireOp",EDGE,"E16.7")])]})});
            var Q5;
            Q5=makeQuery(id+"F5.boolean.opBoolean","COPY",EDGE,{"derivedFrom":makeQuery(id+"F5.opLoft","SWEPT_EDGE",EDGE,{"disambiguationData":[OSD([sQuery(id+"F2.wireOp",EDGE,"E9.4"),sQuery(id+"F2.wireOp",EDGE,"E9.5"),sQuery(id+"F4.wireOp",EDGE,"E16.4"),sQuery(id+"F4.wireOp",EDGE,"E16.5")])]})});
            var Q6;
            {var subQ0=sQuery(id+"F6.wireOp",EDGE,"E18");Q6=makeQuery(id+"F9.boolean.opBoolean","SPLIT",EDGE,{"disambiguationData":[TD([makeQuery(id+"F7.boolean.opBoolean","COPY",FACE,{"derivedFrom":makeQuery(id+"F7.opExtrude","SWEPT_FACE",FACE,{"disambiguationData":[OSD([sQuery(id+"F6.wireOp",EDGE,"E22.bottom")])]})})])],"derivedFrom":makeQuery(id+"F7.boolean.opBoolean","COPY",EDGE,{"derivedFrom":makeQuery(id+"F7.opExtrude","CAP_EDGE",EDGE,{"disambiguationData":[OSD([subQ0])],"isStart":true})})});}
            var Q7;
            Q7=makeQuery(id+"F7.boolean.opBoolean","COPY",EDGE,{"derivedFrom":makeQuery(id+"F7.opExtrude","CAP_EDGE",EDGE,{"disambiguationData":[OSD([sQuery(id+"F6.wireOp",EDGE,"E20.bottom")])],"isStart":true})});
            var Q8;
            Q8=makeQuery(id+"F7.boolean.opBoolean","COPY",EDGE,{"derivedFrom":makeQuery(id+"F7.opExtrude","CAP_EDGE",EDGE,{"disambiguationData":[OSD([sQuery(id+"F6.wireOp",EDGE,"E20.top")])],"isStart":true})});
            var Q9;
            {var subQ0=sQuery(id+"F6.wireOp",EDGE,"E20.left");Q9=makeQuery(id+"F11.boolean.opBoolean","SPLIT",EDGE,{"disambiguationData":[TD([makeQuery(id+"F7.boolean.opBoolean","COPY",FACE,{"derivedFrom":makeQuery(id+"F7.opExtrude","SWEPT_FACE",FACE,{"disambiguationData":[OSD([sQuery(id+"F6.wireOp",EDGE,"E20.top")])]})})])],"derivedFrom":makeQuery(id+"F7.boolean.opBoolean","COPY",EDGE,{"derivedFrom":makeQuery(id+"F7.opExtrude","CAP_EDGE",EDGE,{"disambiguationData":[OSD([subQ0])],"isStart":true})})});}
            var Q10;
            {var subQ0=sQuery(id+"F6.wireOp",EDGE,"E20.left");Q10=makeQuery(id+"F11.boolean.opBoolean","SPLIT",EDGE,{"disambiguationData":[TD([makeQuery(id+"F7.boolean.opBoolean","COPY",FACE,{"derivedFrom":makeQuery(id+"F7.opExtrude","SWEPT_FACE",FACE,{"disambiguationData":[OSD([sQuery(id+"F6.wireOp",EDGE,"E20.bottom")])]})})])],"derivedFrom":makeQuery(id+"F7.boolean.opBoolean","COPY",EDGE,{"derivedFrom":makeQuery(id+"F7.opExtrude","CAP_EDGE",EDGE,{"disambiguationData":[OSD([subQ0])],"isStart":true})})});}
            var Q11;
            Q11=makeQuery(id+"F18.boolean.opBoolean","INTERSECT",EDGE,{"derivedFrom":[makeQuery(id+"F16.boolean.opBoolean","COPY",FACE,{"derivedFrom":makeQuery(id+"F16.opExtrude","SWEPT_FACE",FACE,{"disambiguationData":[OSD([sQuery(id+"F15.wireOp",EDGE,"E32.top")])]})}),makeQuery(id+"F18.opExtrude","CAP_FACE",FACE,{"disambiguationData":[OSD([sQuery(id+"F17.wireOp",EDGE,"E33.bottom"),sQuery(id+"F17.wireOp",EDGE,"E33.top"),sQuery(id+"F17.wireOp",EDGE,"E33.left"),sQuery(id+"F17.wireOp",EDGE,"E33.right")])],"isStart":false})]});
            var Q12;
            Q12=makeQuery(id+"F18.boolean.opBoolean","INTERSECT",EDGE,{"derivedFrom":[makeQuery(id+"F16.boolean.opBoolean","COPY",FACE,{"derivedFrom":makeQuery(id+"F16.opExtrude","SWEPT_FACE",FACE,{"disambiguationData":[OSD([sQuery(id+"F15.wireOp",EDGE,"E32.bottom")])]})}),makeQuery(id+"F18.opExtrude","CAP_FACE",FACE,{"disambiguationData":[OSD([sQuery(id+"F17.wireOp",EDGE,"E33.bottom"),sQuery(id+"F17.wireOp",EDGE,"E33.top"),sQuery(id+"F17.wireOp",EDGE,"E33.left"),sQuery(id+"F17.wireOp",EDGE,"E33.right")])],"isStart":false})]});
            var Q13;
            Q13=makeQuery(id+"F1.opExtrude","CAP_EDGE",EDGE,{"disambiguationData":[OSD([sQuery(id+"F0.wireOp",EDGE,"E2")])],"isStart":false});
            var Q14;
            {var subQ0=sQuery(id+"F0.wireOp",EDGE,"E2");var subQ1=sQuery(id+"F0.wireOp",EDGE,"E1");Q14=makeQuery(id+"F11.boolean.opBoolean","SPLIT",EDGE,{"disambiguationData":[TD([makeQuery(id+"F1.opExtrude","SWEPT_FACE",FACE,{"disambiguationData":[OSD([subQ1])]})])],"derivedFrom":makeQuery(id+"F1.opExtrude","CAP_EDGE",EDGE,{"disambiguationData":[OSD([subQ0])],"isStart":true})});}
            var Q15;
            {var subQ0=sQuery(id+"F0.wireOp",EDGE,"E3");var subQ1=sQuery(id+"F0.wireOp",EDGE,"E2");Q15=makeQuery(id+"F11.boolean.opBoolean","SPLIT",EDGE,{"disambiguationData":[TD([makeQuery(id+"F1.opExtrude","SWEPT_FACE",FACE,{"disambiguationData":[OSD([subQ0])]})])],"derivedFrom":makeQuery(id+"F1.opExtrude","CAP_EDGE",EDGE,{"disambiguationData":[OSD([subQ1])],"isStart":true})});}
            var Q16;
            Q16=makeQuery(id+"F11.boolean.opBoolean","INTERSECT",EDGE,{"derivedFrom":[makeQuery(id+"F1.opExtrude","SWEPT_FACE",FACE,{"disambiguationData":[OSD([sQuery(id+"F0.wireOp",EDGE,"E2")])]}),makeQuery(id+"F11.opExtrude","CAP_FACE",FACE,{"disambiguationData":[OSD([sQuery(id+"F10.wireOp",EDGE,"E27.bottom"),sQuery(id+"F10.wireOp",EDGE,"E27.top"),sQuery(id+"F10.wireOp",EDGE,"E27.left"),sQuery(id+"F10.wireOp",EDGE,"E27.right")])],"isStart":false})]});
            var Q17;
            Q17=makeQuery(id+"F41.boolean.opBoolean","MERGE",EDGE,{"derivedFrom":[makeQuery(id+"F39.opExtrude","CAP_EDGE",EDGE,{"disambiguationData":[OSD([sQuery(id+"F38.wireOp",EDGE,"E75")])],"isStart":false}),makeQuery(id+"F39.opExtrude","CAP_EDGE",EDGE,{"disambiguationData":[OSD([sQuery(id+"F38.wireOp",EDGE,"E82.trimOffspring")])],"isStart":false}),makeQuery(id+"F41.opExtrude","CAP_EDGE",EDGE,{"disambiguationData":[OSD([sQuery(id+"F40.wireOp",EDGE,"E83")])],"isStart":false})]});
            fillet(context, id + "F43", {"entities" : qUnion([Q0, Q1, Q2, Q3, Q4, Q5, Q6, Q7, Q8, Q9, Q10, Q11, Q12, Q13, Q14, Q15, Q16, Q17]), "radius" : 2 * mm, "tangentPropagation" : true, "allowEdgeOverflow" : false});
        }
        {
            var Q0;
            Q0=makeQuery(id+"F39.boolean.opBoolean","MERGE",FACE,{"derivedFrom":[makeQuery(id+"F37.boolean.opBoolean","MERGE",FACE,{"derivedFrom":[makeQuery(id+"F1.opExtrude","SWEPT_FACE",FACE,{"disambiguationData":[OSD([sQuery(id+"F0.wireOp",EDGE,"E3")])]}),makeQuery(id+"F37.opExtrude","SWEPT_FACE",FACE,{"disambiguationData":[OSD([sQuery(id+"F36.wireOp",EDGE,"E66")])]})]}),makeQuery(id+"F39.opExtrude","SWEPT_FACE",FACE,{"disambiguationData":[OSD([sQuery(id+"F38.wireOp",EDGE,"E78")])]})]});
            var sketch = newSketch(context, id + "F44", { "sketchPlane" : qUnion([Q0])});
            skLineSegment(sketch, "E84.bottom", {"start": v(50, -33.74) * mm, "end": v(46, -33.74) * mm});
            skLineSegment(sketch, "E84.top", {"start": v(50, -29.74) * mm, "end": v(46, -29.74) * mm});
            skLineSegment(sketch, "E84.left", {"start": v(50, -33.74) * mm, "end": v(50, -29.74) * mm});
            skLineSegment(sketch, "E84.right", {"start": v(46, -33.74) * mm, "end": v(46, -29.74) * mm});
            skLineSegment(sketch, "E85.MirrorCS", {"start": v(-50, -29.74) * mm, "end": v(-46, -29.74) * mm});
            skLineSegment(sketch, "E86.MirrorCS", {"start": v(-46, -33.74) * mm, "end": v(-46, -29.74) * mm});
            skLineSegment(sketch, "E87.MirrorCS", {"start": v(-50, -33.74) * mm, "end": v(-46, -33.74) * mm});
            skLineSegment(sketch, "E88.MirrorCS", {"start": v(-50, -33.74) * mm, "end": v(-50, -29.74) * mm});
            skSolve(sketch);
        }
        {
            var Q0;
            Q0=qSketchRegion(id+"F44",true);
            extrude(context, id + "F45", {"entities" : qUnion([Q0]), "operationType" : NewBodyOperationType.ADD, "depth" : 5 * mm});
        }
        {
            var Q0;
            Q0=makeQuery(id+"F45.opExtrude","CAP_EDGE",EDGE,{"disambiguationData":[OSD([sQuery(id+"F44.wireOp",EDGE,"E87.MirrorCS")])],"isStart":false});
            var Q1;
            Q1=makeQuery(id+"F45.opExtrude","CAP_EDGE",EDGE,{"disambiguationData":[OSD([sQuery(id+"F44.wireOp",EDGE,"E86.MirrorCS")])],"isStart":false});
            var Q2;
            Q2=makeQuery(id+"F45.opExtrude","CAP_EDGE",EDGE,{"disambiguationData":[OSD([sQuery(id+"F44.wireOp",EDGE,"E88.MirrorCS")])],"isStart":false});
            var Q3;
            Q3=makeQuery(id+"F45.opExtrude","CAP_EDGE",EDGE,{"disambiguationData":[OSD([sQuery(id+"F44.wireOp",EDGE,"E85.MirrorCS")])],"isStart":false});
            var Q4;
            Q4=makeQuery(id+"F45.opExtrude","CAP_EDGE",EDGE,{"disambiguationData":[OSD([sQuery(id+"F44.wireOp",EDGE,"E84.left")])],"isStart":false});
            var Q5;
            Q5=makeQuery(id+"F45.opExtrude","CAP_EDGE",EDGE,{"disambiguationData":[OSD([sQuery(id+"F44.wireOp",EDGE,"E84.bottom")])],"isStart":false});
            var Q6;
            Q6=makeQuery(id+"F45.opExtrude","CAP_EDGE",EDGE,{"disambiguationData":[OSD([sQuery(id+"F44.wireOp",EDGE,"E84.right")])],"isStart":false});
            var Q7;
            Q7=makeQuery(id+"F45.opExtrude","CAP_EDGE",EDGE,{"disambiguationData":[OSD([sQuery(id+"F44.wireOp",EDGE,"E84.top")])],"isStart":false});
            fillet(context, id + "F46", {"entities" : qUnion([Q0, Q1, Q2, Q3, Q4, Q5, Q6, Q7]), "radius" : 2 * mm, "tangentPropagation" : true, "allowEdgeOverflow" : false});
        }
        {
            var Q0;
            {var subQ4=sQuery(id+"F8.wireOp",EDGE,"E26.0.startCap");Q0=makeQuery(id+"F8.imprint","IMPRINT",FACE,{"disambiguationData":[TD([[makeQuery(id+"F8.imprint","IMPRINT",EDGE,{"derivedFrom":subQ4}),-1.0]])]});}
            var sketch = newSketch(context, id + "F47", { "sketchPlane" : qUnion([Q0])});
            skCircle(sketch, "E89", {"center": v(-13, 47.5) * mm, "radius": 0.75 * mm});
            skCircle(sketch, "E90", {"center": v(-13, 12.5) * mm, "radius": 0.75 * mm});
            skSolve(sketch);
        }
        {
            var Q0;
            Q0=qSketchRegion(id+"F47",true);
            extrude(context, id + "F48", {"entities" : qUnion([Q0]), "operationType" : NewBodyOperationType.REMOVE, "oppositeDirection" : true, "depth" : 10 * mm});
        }
        {
            var Q0;
            {var subQ0=sQuery(id+"F17.wireOp",EDGE,"E33.bottom");var subQ1=sQuery(id+"F17.wireOp",EDGE,"E33.left");var subQ2=sQuery(id+"F17.wireOp",EDGE,"E33.right");Q0=makeQuery(id+"F18.boolean.opBoolean","COPY",FACE,{"disambiguationData":[TD([makeQuery(id+"F16.boolean.opBoolean","COPY",FACE,{"derivedFrom":makeQuery(id+"F16.opExtrude","SWEPT_FACE",FACE,{"disambiguationData":[OSD([sQuery(id+"F15.wireOp",EDGE,"E32.top")])]})})])],"derivedFrom":makeQuery(id+"F18.opExtrude","CAP_FACE",FACE,{"disambiguationData":[OSD([subQ0,sQuery(id+"F17.wireOp",EDGE,"E33.top"),subQ1,subQ2])],"isStart":false})});}
            var sketch = newSketch(context, id + "F49", { "sketchPlane" : qUnion([Q0])});
            skCircle(sketch, "E91", {"center": v(0, -22.74) * mm, "radius": 0.75 * mm});
            skPoint(sketch, "E92", {"position": v(0, -36.74) * mm});
            skCircle(sketch, "E93", {"center": v(0, -50.74) * mm, "radius": 0.75 * mm});
            skPoint(sketch, "E94.orphan", {"position": v(6.5, -23.24) * mm});
            skPoint(sketch, "E95.end.orphan", {"position": v(6.5, -50.24) * mm});
            skPoint(sketch, "E96.end.orphan", {"position": v(-6.5, -50.24) * mm});
            skSolve(sketch);
        }
        {
            var Q0;
            Q0=qSketchRegion(id+"F49",true);
            extrude(context, id + "F50", {"entities" : qUnion([Q0]), "operationType" : NewBodyOperationType.REMOVE, "oppositeDirection" : true, "depth" : 10 * mm});
        }
    });
